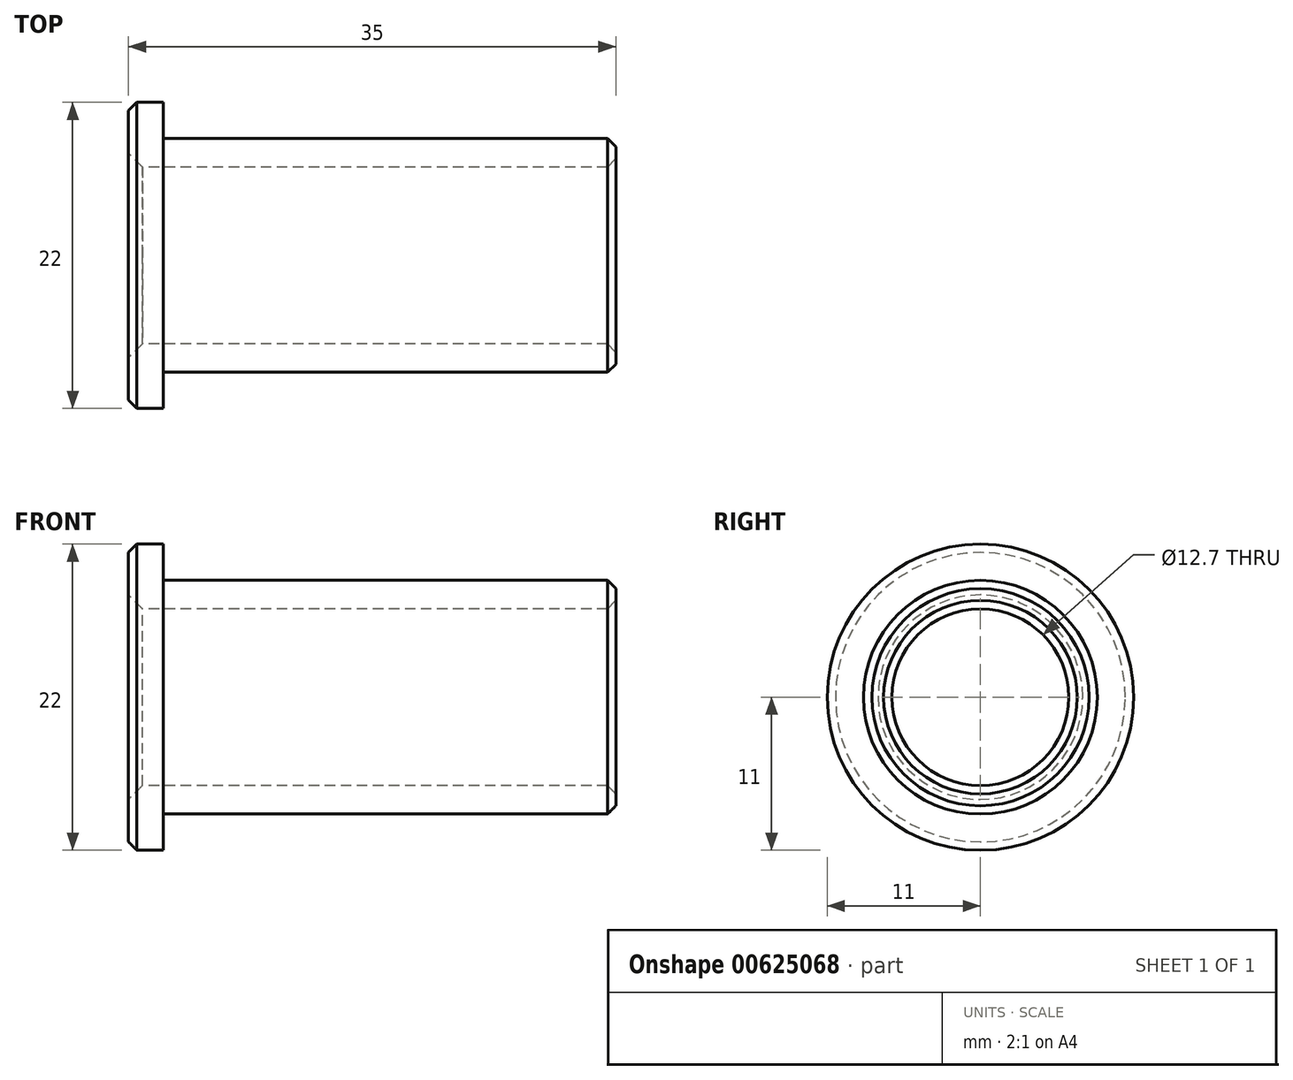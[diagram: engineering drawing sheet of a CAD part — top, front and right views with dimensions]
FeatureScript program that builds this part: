
annotation { "Feature Type Name" : "Feature", "Feature Type Description" : "" }
export const myFeature = defineFeature(function(context is Context, id is Id, definition is map)
    precondition{}
    {
        {
            var Q0;
            Q0=qCreatedBy(makeId("Right.planeOp"),FACE);
            var sketch = newSketch(context, id + "F0", { "sketchPlane" : qUnion([Q0])});
            skCircle(sketch, "E0", {"center": v(0, 0) * mm, "radius": 6.35 * mm});
            skCircle(sketch, "E1", {"center": v(0, 0) * mm, "radius": 8.4 * mm});
            skCircle(sketch, "E2", {"center": v(0, 0) * mm, "radius": 11 * mm});
            skSolve(sketch);
        }
        {
            var Q0;
            Q0 = qSketchRegion(id + "F0", true);
            extrude(context, id + "F1", {"entities" : qUnion([Q0]), "depth" : 2.5 * mm, "offsetDistance" : 25 * mm});
        }
        {
            var Q0;
            Q0=makeQuery(id+"F0.imprint","IMPRINT",FACE,{"disambiguationData":[TD([[makeQuery(id+"F0.imprint","IMPRINT",EDGE,{"derivedFrom":sQuery(id+"F0.wireOp",EDGE,"E0")}),-1.0]])]});
            extrude(context, id + "F2", {"entities" : qUnion([Q0]), "operationType" : NewBodyOperationType.ADD, "depth" : 35 * mm, "offsetDistance" : 25 * mm});
        }
        {
            var Q0;
            Q0=makeQuery(id+"F2.opExtrude","CAP_EDGE",EDGE,{"disambiguationData":[OSD([sQuery(id+"F0.wireOp",EDGE,"E0")])],"isStart":false});
            var Q1;
            Q1=makeQuery(id+"F2.opExtrude","CAP_EDGE",EDGE,{"disambiguationData":[OSD([sQuery(id+"F0.wireOp",EDGE,"E1")])],"isStart":false});
            var Q2;
            Q2=makeQuery(id+"F1.opExtrude","CAP_EDGE",EDGE,{"disambiguationData":[OSD([sQuery(id+"F0.wireOp",EDGE,"E2")])],"isStart":true});
            chamfer(context, id + "F3", {"entities" : qUnion([Q0, Q1, Q2]), "width" : .6 * mm, "tangentPropagation" : true});
        }
        {
            var Q0;
            Q0=makeQuery(id+"F2.opExtrude","CAP_EDGE",EDGE,{"disambiguationData":[OSD([sQuery(id+"F0.wireOp",EDGE,"E0")])],"isStart":true});
            chamfer(context, id + "F4", {"entities" : qUnion([Q0]), "width" : 1 * mm, "tangentPropagation" : true});
        }
    });
